# Revit family: Faucet-Lavatory-KOHLER-Aleo-K-72337ME_1
name_source: partatom
category: Plumbing Fixtures
units: mm (PartAtom-declared; Revit-internal decimal feet)

## family parameters
Cut with Voids When Loaded = No
Host = Face
OmniClass Number = 23.31.11.00
OmniClass Title = Faucets
Part Type = Normal
Room Calculation Point = No
Round Connector Dimension = Use Diameter
Shared = No

## types (2) — shared parameters
ADA Compliant = No
Assembly Code = D2010
CW Connection = Yes
Cold Water Inlet = Cold Water Inlet
Date Modified = 04/29/2023
Default Elevation = 36"
Description = Tall Lavetory Faucet Without Drain
Drain Included = No
Flow Rate = 1 GPM
HW Connection = Yes
Handle Clearance = 4 9/16"
Height = 10 9/16"
Hot Water Inlet = Hot Water Inlet
Length = 6 1/4"
Manufacturer = Kohler Co.
Master Format 2014 = 22 41 39
Master Format 2014 Name = Residential Faucets, Supplies, and Trim
Material = Premium Metal Construction
Pressure = 0.00 psi
Product Name = Aleo
Spout Reach = 6 1/4"
URL = https://me.kohler.com
Vent Connection = No
Waste Connection = No
Waste Water Outlet = Waste Water Outlet
WaterSense Certified = No
Width = 2"

## per-type parameters (varying)
| type | Finish | Model | Secondary Finish | Type |
| AF-Vibrant French Gold | Kohler-Metal-AF-Vibrant_French_Gold | K-72337ME-4ND-AF | Kohler-Metal-AF-Vibrant_French_Gold | 1 |
| BL-Matte Black | Kohler-Metal-BL-Matte_Black | K-72337ME-4ND-BL | Kohler-Metal-CP-Polished_Chrome | 2 |

## geometry (parser evidence)
native form markers: Sweep x4
no freeform markers — native parametric forms only
